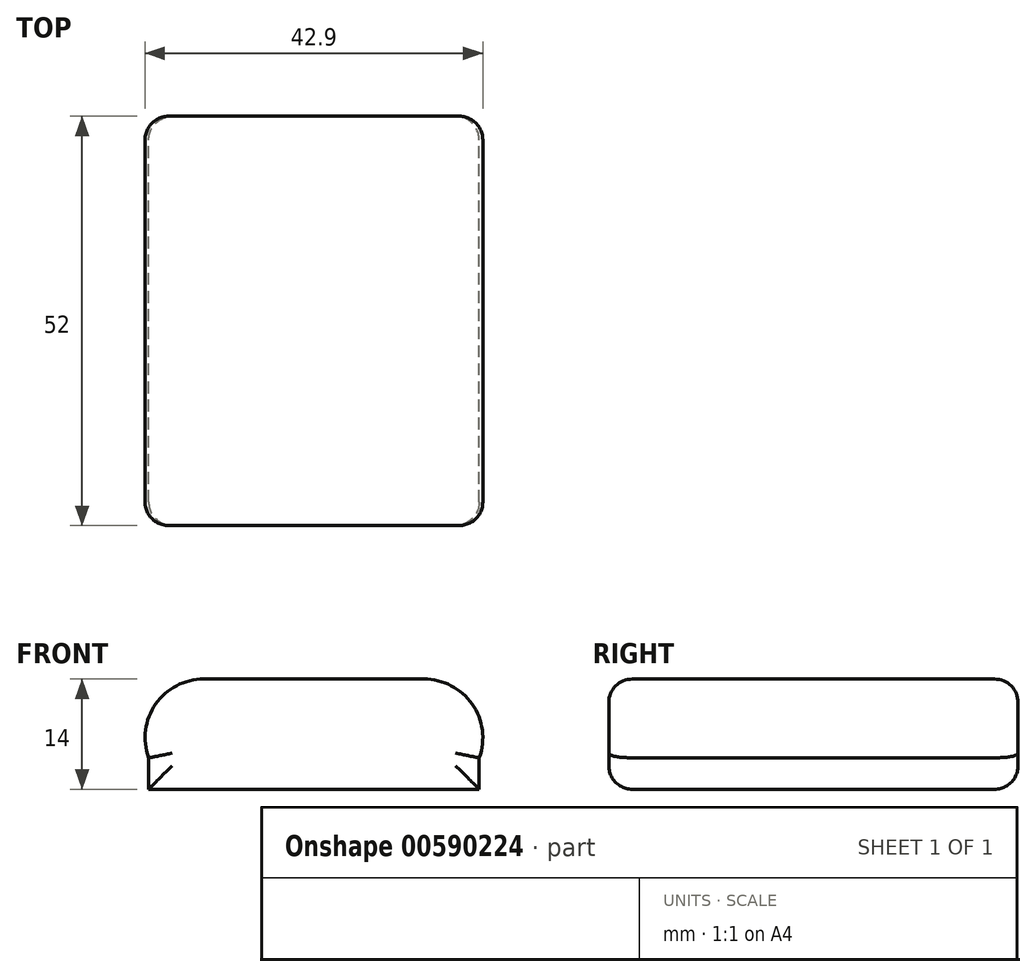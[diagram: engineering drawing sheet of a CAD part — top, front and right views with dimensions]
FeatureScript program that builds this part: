
annotation { "Feature Type Name" : "Feature", "Feature Type Description" : "" }
export const myFeature = defineFeature(function(context is Context, id is Id, definition is map)
    precondition{}
    {
        {
            var Q0;
            Q0=qCreatedBy(makeId("Front.planeOp"),FACE);
            var sketch = newSketch(context, id + "F0", { "sketchPlane" : qUnion([Q0])});
            skLineSegment(sketch, "E0.bottom", {"start": v(14, -7) * mm, "end": v(-14, -7) * mm});
            skLineSegment(sketch, "E0.top", {"start": v(14, 7) * mm, "end": v(-14, 7) * mm});
            skLineSegment(sketch, "E0.left", {"start": v(14, -7) * mm, "end": v(14, 7) * mm});
            skLineSegment(sketch, "E0.right", {"start": v(-14, -7) * mm, "end": v(-14, 7) * mm});
            skPoint(sketch, "E0.middle", {"position": v(0, 0) * mm});
            skLineSegment(sketch, "E1", {"start": v(-14, -7) * mm, "end": v(-21, -7) * mm});
            skLineSegment(sketch, "E2", {"start": v(14, -7) * mm, "end": v(21, -7) * mm});
            skLineSegment(sketch, "E3", {"start": v(-21, -7) * mm, "end": v(-21, -3) * mm});
            skLineSegment(sketch, "E4", {"start": v(21, -7) * mm, "end": v(21, -3) * mm});
            skArc(sketch, "E5", {"start": v(-14, 7) * mm, "mid": v(-20.1, 3.82) * mm, "end": v(-21, -3) * mm});
            skArc(sketch, "E6", {"start": v(21, -3) * mm, "mid": v(20.1, 3.82) * mm, "end": v(14, 7) * mm});
            skSolve(sketch);
        }
        {
            var Q0;
            Q0 = qSketchRegion(id + "F0", true);
            extrude(context, id + "F1", {"entities" : qUnion([Q0]), "depth" : 52 * mm, "offsetDistance" : 25 * mm});
        }
        {
            var Q0;
            Q0=makeQuery(id+"F1.opExtrude","CAP_FACE",FACE,{"disambiguationData":[OSD([sQuery(id+"F0.wireOp",EDGE,"E0.bottom"),sQuery(id+"F0.wireOp",EDGE,"E0.top"),sQuery(id+"F0.wireOp",EDGE,"E1"),sQuery(id+"F0.wireOp",EDGE,"E2"),sQuery(id+"F0.wireOp",EDGE,"E3"),sQuery(id+"F0.wireOp",EDGE,"E4"),sQuery(id+"F0.wireOp",EDGE,"stta9PV9-G0h3-lKJE-htm5-4mhzk5wmezgI"),sQuery(id+"F0.wireOp",EDGE,"O8ZtQp2x-5TGG-lX6x-Sl6Y-NY4k2NN79q24")])],"isStart":false});
            fillet(context, id + "F2", {"entities" : qUnion([Q0]), "radius" : 3 * mm, "tangentPropagation" : true, "allowEdgeOverflow" : false});
        }
        {
            var Q0;
            Q0=makeQuery(id+"F1.opExtrude","CAP_FACE",FACE,{"disambiguationData":[OSD([sQuery(id+"F0.wireOp",EDGE,"E0.bottom"),sQuery(id+"F0.wireOp",EDGE,"E0.top"),sQuery(id+"F0.wireOp",EDGE,"E1"),sQuery(id+"F0.wireOp",EDGE,"E2"),sQuery(id+"F0.wireOp",EDGE,"E3"),sQuery(id+"F0.wireOp",EDGE,"E4"),sQuery(id+"F0.wireOp",EDGE,"E5"),sQuery(id+"F0.wireOp",EDGE,"E6")])],"isStart":true});
            fillet(context, id + "F3", {"entities" : qUnion([Q0]), "radius" : 3 * mm, "tangentPropagation" : true, "allowEdgeOverflow" : false});
        }
    });
